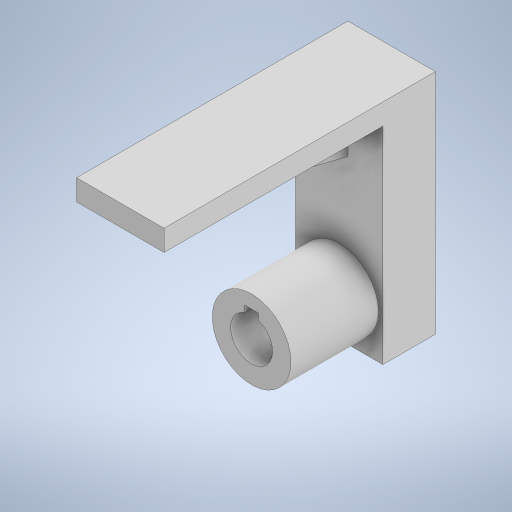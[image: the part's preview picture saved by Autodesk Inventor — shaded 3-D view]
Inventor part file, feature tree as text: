
AUTODESK INVENTOR PART (.ipt)
format: ipt  version: 2024 (Build 280153000, 153)  size: 284,672 bytes
history: native  units: in
note: dims shown in document units (in); Inventor stores cm internally (conversion verified against a paired STEP export)
features: sketch x6, extrude x5, rib x1
ambient origin geometry x8: Origin, YZ Plane, XZ Plane, XY Plane, X Axis, Y Axis, Z Axis, Center Point
bodies: Body1 (feature_tree)
feature tree (12):
  extrude  "Extrusion8"  Depth=1.9685in TaperAngle=0.0deg
  extrude  "Extrusion9"  Depth=0.5906in
  extrude  "Extrusion10"  Depth=0.1575in
  extrude  "Extrusion11"  Depth=1.5748in TaperAngle=0.0deg
  extrude  "Extrusion12"  Depth=1.9685in
  rib  "Rib2"
  sketch  "Sketch7"  dims[d33=1.7717in d34=1.9685in d35=0.0in]
  sketch  "Sketch8"  dims[d36=0.9449in d37=0.5906in]
  sketch  "Sketch9"  dims[d38=0.1575in d39=0.1575in]
  sketch  "Sketch10"  dims[d40=0.1451in d41=1.5748in d42=0.0in]
  sketch  "Sketch11"  dims[d43=1.9685in d44=1.9685in]
  sketch  "Sketch14"  dims[d45=1.1811in d46=0.0in d47=3.1496in d48=0.0in d49=0.4724in d50=4.9213in d51=0.0in d70=0.9843in d71=0.7149in d72=3.937in d73=0.0394in d74=0.3937in d75=0.0in d76=0.0in d77=0.0394in d78=0.0394in]
